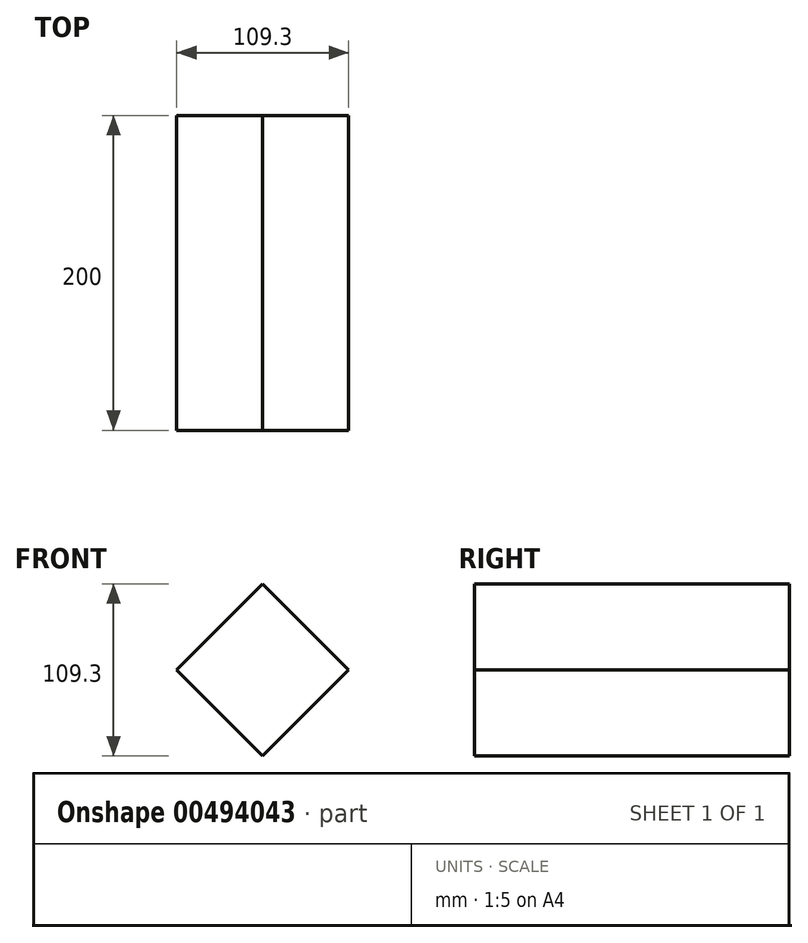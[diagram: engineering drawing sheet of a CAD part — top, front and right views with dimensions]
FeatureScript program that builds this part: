
annotation { "Feature Type Name" : "Feature", "Feature Type Description" : "" }
export const myFeature = defineFeature(function(context is Context, id is Id, definition is map)
    precondition{}
    {
        {
            var Q0;
            Q0=qCreatedBy(makeId("Front.planeOp"),FACE);
            var sketch = newSketch(context, id + "F0", { "sketchPlane" : qUnion([Q0])});
            skCircle(sketch, "E0.cCircle", {"center": v(0, 0) * mm, "radius": 54.65 * mm, "construction": true});
            skLineSegment(sketch, "E0.0", {"start": v(0, 54.65) * mm, "end": v(54.65, 0) * mm});
            skLineSegment(sketch, "E0.1", {"start": v(54.65, 0) * mm, "end": v(0, -54.65) * mm});
            skLineSegment(sketch, "E0.2", {"start": v(0, -54.65) * mm, "end": v(-54.65, 0) * mm});
            skLineSegment(sketch, "E0.3", {"start": v(-54.65, 0) * mm, "end": v(0, 54.65) * mm});
            skSolve(sketch);
        }
        {
            var Q0;
            Q0=makeQuery(id+"F0.imprint","IMPRINT",FACE,{"disambiguationData":[TD([[makeQuery(id+"F0.imprint","IMPRINT",EDGE,{"derivedFrom":sQuery(id+"F0.wireOp",EDGE,"E0.0")}),-1.0]])]});
            extrude(context, id + "F1", {"entities" : qUnion([Q0]), "depth" : 200 * mm});
        }
    });
